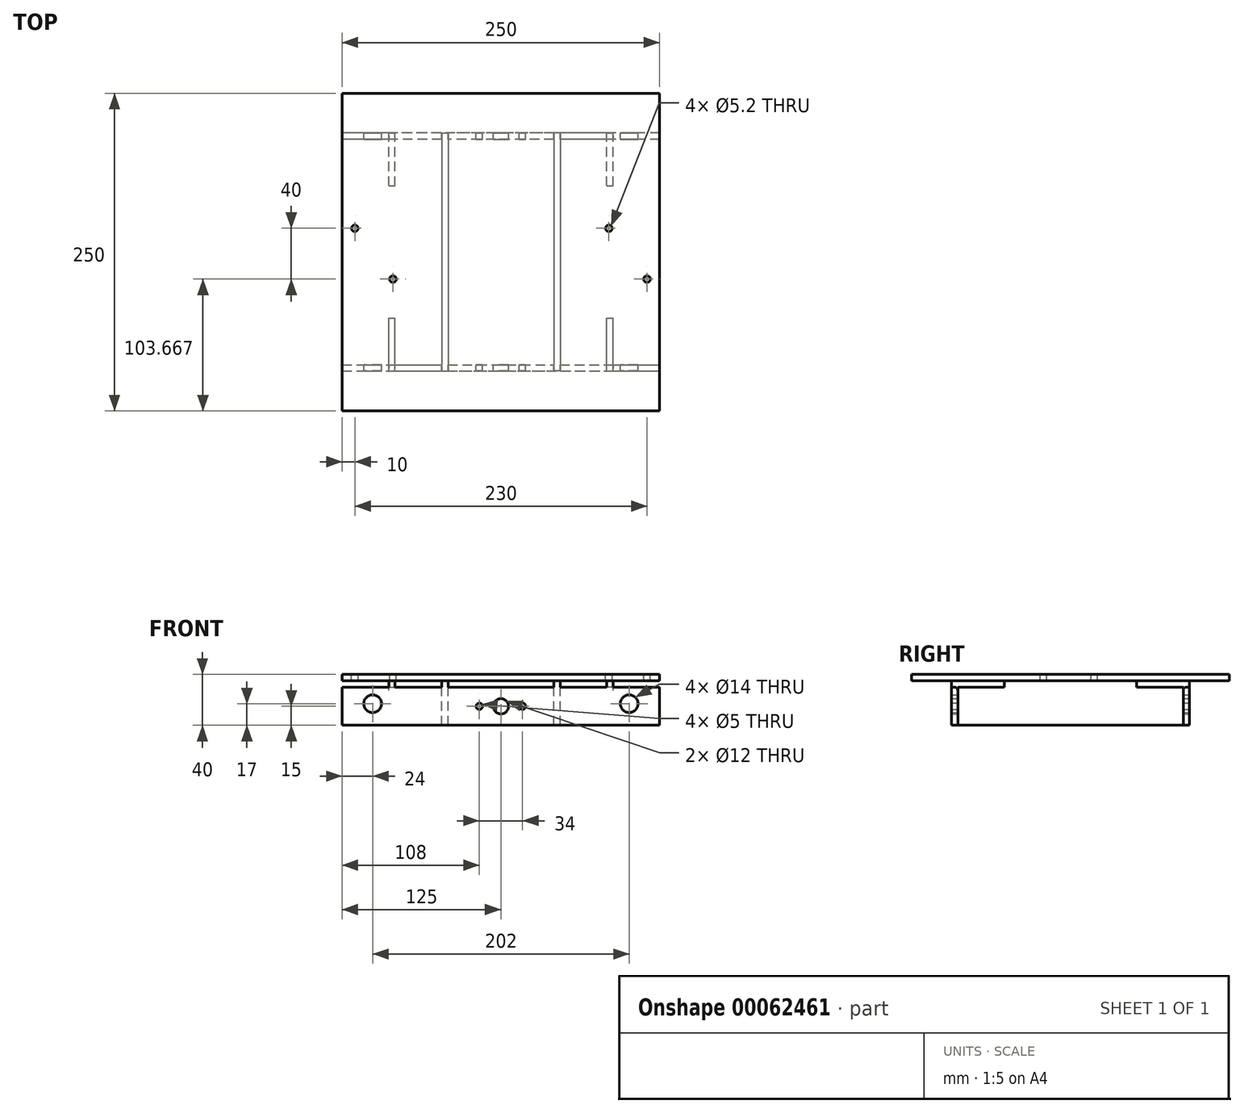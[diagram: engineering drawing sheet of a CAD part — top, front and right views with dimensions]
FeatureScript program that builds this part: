
annotation { "Feature Type Name" : "Feature", "Feature Type Description" : "" }
export const myFeature = defineFeature(function(context is Context, id is Id, definition is map)
    precondition{}
    {
        {
            assignVariable(context, id + "F0", {"name" : "BASE_THICKNESS", "anyValue" : 5});
        }
        {
            assignVariable(context, id + "F1", {"name" : "FLANGE_OFFSET", "anyValue" : 5});
        }
        {
            var Q0;
            Q0=qCreatedBy(makeId("Top.planeOp"),FACE);
            var sketch = newSketch(context, id + "F2", { "sketchPlane" : qUnion([Q0])});
            skLineSegment(sketch, "E0.rect.bottom", {"start": v(125, -125) * mm, "end": v(-125, -125) * mm});
            skLineSegment(sketch, "E0.rect.top", {"start": v(125, 125) * mm, "end": v(-125, 125) * mm});
            skLineSegment(sketch, "E0.rect.left", {"start": v(125, -125) * mm, "end": v(125, 125) * mm});
            skLineSegment(sketch, "E0.rect.right", {"start": v(-125, -125) * mm, "end": v(-125, 125) * mm});
            skPoint(sketch, "E0.rect.middle", {"position": v(0, 0) * mm});
            skSolve(sketch);
        }
        {
            var Q0;
            Q0 = qSketchRegion(id + "F2", true);
            extrude(context, id + "F3", {"entities" : qUnion([Q0]), "depth" : (getVariable(context, 'BASE_THICKNESS')) * mm});
        }
        {
            var Q0;
            Q0=makeQuery(id+"F3.opExtrude","CAP_FACE",FACE,{"disambiguationData":[OSD([sQuery(id+"F2.wireOp",EDGE,"E0.rect.bottom"),sQuery(id+"F2.wireOp",EDGE,"E0.rect.top"),sQuery(id+"F2.wireOp",EDGE,"E0.rect.left"),sQuery(id+"F2.wireOp",EDGE,"E0.rect.right")])],"isStart":true});
            var sketch = newSketch(context, id + "F4", { "sketchPlane" : qUnion([Q0])});
            skLineSegment(sketch, "E1.bottom", {"start": v(-88.33, 93.75) * mm, "end": v(-83.33, 93.75) * mm});
            skLineSegment(sketch, "E1.top", {"start": v(-88.33, 52.08) * mm, "end": v(-83.33, 52.08) * mm});
            skLineSegment(sketch, "E1.left", {"start": v(-88.33, 93.75) * mm, "end": v(-88.33, 52.08) * mm});
            skLineSegment(sketch, "E1.right", {"start": v(-83.33, 93.75) * mm, "end": v(-83.33, 52.08) * mm});
            skLineSegment(sketch, "E2.bottom", {"start": v(83.33, 93.75) * mm, "end": v(88.33, 93.75) * mm});
            skLineSegment(sketch, "E2.top", {"start": v(83.33, 52.08) * mm, "end": v(88.33, 52.08) * mm});
            skLineSegment(sketch, "E2.left", {"start": v(83.33, 93.75) * mm, "end": v(83.33, 52.08) * mm});
            skLineSegment(sketch, "E2.right", {"start": v(88.33, 93.75) * mm, "end": v(88.33, 52.08) * mm});
            skLineSegment(sketch, "E3.bottom", {"start": v(-88.33, -52.08) * mm, "end": v(-83.33, -52.08) * mm});
            skLineSegment(sketch, "E3.top", {"start": v(-88.33, -93.75) * mm, "end": v(-83.33, -93.75) * mm});
            skLineSegment(sketch, "E3.left", {"start": v(-88.33, -52.08) * mm, "end": v(-88.33, -93.75) * mm});
            skLineSegment(sketch, "E3.right", {"start": v(-83.33, -52.08) * mm, "end": v(-83.33, -93.75) * mm});
            skLineSegment(sketch, "E4.bottom", {"start": v(83.33, -52.08) * mm, "end": v(88.33, -52.08) * mm});
            skLineSegment(sketch, "E4.top", {"start": v(83.33, -93.75) * mm, "end": v(88.33, -93.75) * mm});
            skLineSegment(sketch, "E4.left", {"start": v(83.33, -52.08) * mm, "end": v(83.33, -93.75) * mm});
            skLineSegment(sketch, "E4.right", {"start": v(88.33, -52.08) * mm, "end": v(88.33, -93.75) * mm});
            skSolve(sketch);
        }
        {
            var Q0;
            Q0 = qSketchRegion(id + "F4", true);
            extrude(context, id + "F5", {"entities" : qUnion([Q0]), "operationType" : NewBodyOperationType.ADD, "depth" : (getVariable(context, 'FLANGE_OFFSET')) * mm});
        }
        {
            var Q0;
            Q0=makeQuery(id+"F5.opExtrude","SWEPT_FACE",FACE,{"disambiguationData":[OSD([sQuery(id+"F4.wireOp",EDGE,"E4.top")])]});
            var sketch = newSketch(context, id + "F6", { "sketchPlane" : qUnion([Q0])});
            skLineSegment(sketch, "E5.bottom", {"start": v(-125, -5) * mm, "end": v(125, -5) * mm});
            skLineSegment(sketch, "E5.top", {"start": v(-125, -35) * mm, "end": v(125, -35) * mm});
            skLineSegment(sketch, "E5.left", {"start": v(-125, -5) * mm, "end": v(-125, -35) * mm});
            skLineSegment(sketch, "E5.right", {"start": v(125, -5) * mm, "end": v(125, -35) * mm});
            skSolve(sketch);
        }
        {
            var Q0;
            Q0 = qSketchRegion(id + "F6", true);
            extrude(context, id + "F7", {"entities" : qUnion([Q0]), "operationType" : NewBodyOperationType.ADD, "oppositeDirection" : true, "depth" : (getVariable(context, 'BASE_THICKNESS')) * mm});
        }
        {
            var Q0;
            Q0=makeQuery(id+"F5.opExtrude","SWEPT_FACE",FACE,{"disambiguationData":[OSD([sQuery(id+"F4.wireOp",EDGE,"E1.bottom")])]});
            var sketch = newSketch(context, id + "F8", { "sketchPlane" : qUnion([Q0])});
            skPoint(sketch, "E6.firstSnap0", {"position": v(-85.83, -5) * mm});
            skLineSegment(sketch, "E6.bottom", {"start": v(-125, -5) * mm, "end": v(125, -5) * mm});
            skLineSegment(sketch, "E6.top", {"start": v(-125, -35) * mm, "end": v(125, -35) * mm});
            skLineSegment(sketch, "E6.left", {"start": v(-125, -5) * mm, "end": v(-125, -35) * mm});
            skLineSegment(sketch, "E6.right", {"start": v(125, -5) * mm, "end": v(125, -35) * mm});
            skSolve(sketch);
        }
        {
            var Q0;
            Q0 = qSketchRegion(id + "F8", true);
            extrude(context, id + "F9", {"entities" : qUnion([Q0]), "operationType" : NewBodyOperationType.ADD, "oppositeDirection" : true, "depth" : (getVariable(context, 'BASE_THICKNESS')) * mm});
        }
        {
            var Q0;
            Q0=makeQuery(id+"F3.opExtrude","CAP_FACE",FACE,{"disambiguationData":[OSD([sQuery(id+"F2.wireOp",EDGE,"E0.rect.bottom"),sQuery(id+"F2.wireOp",EDGE,"E0.rect.top"),sQuery(id+"F2.wireOp",EDGE,"E0.rect.left"),sQuery(id+"F2.wireOp",EDGE,"E0.rect.right")])],"isStart":true});
            var sketch = newSketch(context, id + "F10", { "sketchPlane" : qUnion([Q0])});
            skLineSegment(sketch, "E7.rect.bottom", {"start": v(46.67, -93.75) * mm, "end": v(41.67, -93.75) * mm});
            skLineSegment(sketch, "E7.rect.top", {"start": v(46.67, 93.75) * mm, "end": v(41.67, 93.75) * mm});
            skLineSegment(sketch, "E7.rect.left", {"start": v(46.67, -93.75) * mm, "end": v(46.67, 93.75) * mm});
            skLineSegment(sketch, "E7.rect.right", {"start": v(41.67, -93.75) * mm, "end": v(41.67, 93.75) * mm});
            skPoint(sketch, "E7.rect.middle", {"position": v(0, 0) * mm});
            skLineSegment(sketch, "E8.MirrorCS", {"start": v(-46.67, -93.75) * mm, "end": v(-46.67, 93.75) * mm});
            skLineSegment(sketch, "E9.MirrorCS", {"start": v(-41.67, -93.75) * mm, "end": v(-41.67, 93.75) * mm});
            skLineSegment(sketch, "E10.MirrorCS", {"start": v(-46.67, -93.75) * mm, "end": v(-41.67, -93.75) * mm});
            skLineSegment(sketch, "E11.MirrorCS", {"start": v(-46.67, 93.75) * mm, "end": v(-41.67, 93.75) * mm});
            skLineSegment(sketch, "E12", {"start": v(46.67, 93.75) * mm, "end": v(41.67, -93.75) * mm, "construction": true});
            skLineSegment(sketch, "E13", {"start": v(41.67, 93.75) * mm, "end": v(46.67, -93.75) * mm, "construction": true});
            skPoint(sketch, "E14", {"position": v(44.17, 0) * mm});
            skSolve(sketch);
        }
        {
            var Q0;
            {var subQ0=sQuery(id+"F8.wireOp",EDGE,"E6.bottom");var subQ1=sQuery(id+"F4.wireOp",EDGE,"E2.right");var subQ2=sQuery(id+"F4.wireOp",EDGE,"E2.left");Q0=makeQuery(id+"F9.boolean.opBoolean","SPLIT",EDGE,{"disambiguationData":[TD([makeQuery(id+"F5.opExtrude","CAP_FACE",FACE,{"disambiguationData":[OSD([sQuery(id+"F4.wireOp",EDGE,"E2.bottom"),sQuery(id+"F4.wireOp",EDGE,"E2.top"),subQ2,subQ1])],"isStart":false}),makeQuery(id+"F5.opExtrude","SWEPT_FACE",FACE,{"disambiguationData":[OSD([subQ2])]}),makeQuery(id+"F5.opExtrude","SWEPT_FACE",FACE,{"disambiguationData":[OSD([subQ1])]}),makeQuery(id+"F9.opExtrude","SWEPT_FACE",FACE,{"disambiguationData":[OSD([subQ0])]}),makeQuery(id+"F9.opExtrude","CAP_FACE",FACE,{"disambiguationData":[OSD([subQ0,sQuery(id+"F8.wireOp",EDGE,"E6.top"),sQuery(id+"F8.wireOp",EDGE,"E6.left"),sQuery(id+"F8.wireOp",EDGE,"E6.right")])],"isStart":false})])],"derivedFrom":makeQuery(id+"F9.opExtrude","CAP_EDGE",EDGE,{"disambiguationData":[OSD([subQ0])],"isStart":false})});}
            var Q1;
            {var subQ0=sQuery(id+"F8.wireOp",EDGE,"E6.bottom");var subQ1=sQuery(id+"F4.wireOp",EDGE,"E1.right");var subQ2=sQuery(id+"F4.wireOp",EDGE,"E1.left");Q1=makeQuery(id+"F9.boolean.opBoolean","SPLIT",EDGE,{"disambiguationData":[TD([makeQuery(id+"F5.opExtrude","CAP_FACE",FACE,{"disambiguationData":[OSD([sQuery(id+"F4.wireOp",EDGE,"E1.bottom"),sQuery(id+"F4.wireOp",EDGE,"E1.top"),subQ2,subQ1])],"isStart":false}),makeQuery(id+"F5.opExtrude","SWEPT_FACE",FACE,{"disambiguationData":[OSD([subQ2])]}),makeQuery(id+"F5.opExtrude","SWEPT_FACE",FACE,{"disambiguationData":[OSD([subQ1])]}),makeQuery(id+"F9.opExtrude","SWEPT_FACE",FACE,{"disambiguationData":[OSD([subQ0])]}),makeQuery(id+"F9.opExtrude","CAP_FACE",FACE,{"disambiguationData":[OSD([subQ0,sQuery(id+"F8.wireOp",EDGE,"E6.top"),sQuery(id+"F8.wireOp",EDGE,"E6.left"),sQuery(id+"F8.wireOp",EDGE,"E6.right")])],"isStart":false})])],"derivedFrom":makeQuery(id+"F9.opExtrude","CAP_EDGE",EDGE,{"disambiguationData":[OSD([subQ0])],"isStart":false})});}
            var Q2;
            {var subQ0=sQuery(id+"F6.wireOp",EDGE,"E5.bottom");var subQ1=sQuery(id+"F4.wireOp",EDGE,"E4.right");var subQ2=sQuery(id+"F4.wireOp",EDGE,"E4.left");Q2=makeQuery(id+"F7.boolean.opBoolean","SPLIT",EDGE,{"disambiguationData":[TD([makeQuery(id+"F5.opExtrude","CAP_FACE",FACE,{"disambiguationData":[OSD([sQuery(id+"F4.wireOp",EDGE,"E4.bottom"),sQuery(id+"F4.wireOp",EDGE,"E4.top"),subQ2,subQ1])],"isStart":false}),makeQuery(id+"F5.opExtrude","SWEPT_FACE",FACE,{"disambiguationData":[OSD([subQ2])]}),makeQuery(id+"F5.opExtrude","SWEPT_FACE",FACE,{"disambiguationData":[OSD([subQ1])]}),makeQuery(id+"F7.opExtrude","SWEPT_FACE",FACE,{"disambiguationData":[OSD([subQ0])]}),makeQuery(id+"F7.opExtrude","CAP_FACE",FACE,{"disambiguationData":[OSD([subQ0,sQuery(id+"F6.wireOp",EDGE,"E5.top"),sQuery(id+"F6.wireOp",EDGE,"E5.left"),sQuery(id+"F6.wireOp",EDGE,"E5.right")])],"isStart":false})])],"derivedFrom":makeQuery(id+"F7.opExtrude","CAP_EDGE",EDGE,{"disambiguationData":[OSD([subQ0])],"isStart":false})});}
            var Q3;
            {var subQ0=sQuery(id+"F6.wireOp",EDGE,"E5.bottom");var subQ1=sQuery(id+"F4.wireOp",EDGE,"E3.right");var subQ2=sQuery(id+"F4.wireOp",EDGE,"E3.left");Q3=makeQuery(id+"F7.boolean.opBoolean","SPLIT",EDGE,{"disambiguationData":[TD([makeQuery(id+"F5.opExtrude","CAP_FACE",FACE,{"disambiguationData":[OSD([sQuery(id+"F4.wireOp",EDGE,"E3.bottom"),sQuery(id+"F4.wireOp",EDGE,"E3.top"),subQ2,subQ1])],"isStart":false}),makeQuery(id+"F5.opExtrude","SWEPT_FACE",FACE,{"disambiguationData":[OSD([subQ2])]}),makeQuery(id+"F5.opExtrude","SWEPT_FACE",FACE,{"disambiguationData":[OSD([subQ1])]}),makeQuery(id+"F7.opExtrude","SWEPT_FACE",FACE,{"disambiguationData":[OSD([subQ0])]}),makeQuery(id+"F7.opExtrude","CAP_FACE",FACE,{"disambiguationData":[OSD([subQ0,sQuery(id+"F6.wireOp",EDGE,"E5.top"),sQuery(id+"F6.wireOp",EDGE,"E5.left"),sQuery(id+"F6.wireOp",EDGE,"E5.right")])],"isStart":false})])],"derivedFrom":makeQuery(id+"F7.opExtrude","CAP_EDGE",EDGE,{"disambiguationData":[OSD([subQ0])],"isStart":false})});}
            fillet(context, id + "F11", {"entities" : qUnion([Q0, Q1, Q2, Q3]), "radius" : (getVariable(context, 'BASE_THICKNESS')) / 2 * mm, "tangentPropagation" : true, "allowEdgeOverflow" : false});
        }
        {
            var Q0;
            Q0 = qSketchRegion(id + "F10", true);
            var Q1;
            Q1=makeQuery(id+"F9.opExtrude","SWEPT_FACE",FACE,{"disambiguationData":[OSD([sQuery(id+"F8.wireOp",EDGE,"E6.top")])]});
            extrude(context, id + "F12", {"entities" : qUnion([Q0]), "operationType" : NewBodyOperationType.ADD, "endBound" : BoundingType.UP_TO_SURFACE, "endBoundEntityFace" : qUnion([Q1]), "depth" : 25 * mm});
        }
        {
            var Q0;
            Q0=makeQuery(id+"F12.boolean.opBoolean","MERGE",FACE,{"derivedFrom":[makeQuery(id+"F7.boolean.opBoolean","MERGE",FACE,{"derivedFrom":[makeQuery(id+"F5.opExtrude","SWEPT_FACE",FACE,{"disambiguationData":[OSD([sQuery(id+"F4.wireOp",EDGE,"E3.top")])]}),makeQuery(id+"F5.opExtrude","SWEPT_FACE",FACE,{"disambiguationData":[OSD([sQuery(id+"F4.wireOp",EDGE,"E4.top")])]}),makeQuery(id+"F7.opExtrude","CAP_FACE",FACE,{"disambiguationData":[OSD([sQuery(id+"F6.wireOp",EDGE,"E5.bottom"),sQuery(id+"F6.wireOp",EDGE,"E5.top"),sQuery(id+"F6.wireOp",EDGE,"E5.left"),sQuery(id+"F6.wireOp",EDGE,"E5.right")])],"isStart":true})]}),makeQuery(id+"F12.opExtrude","SWEPT_FACE",FACE,{"disambiguationData":[OSD([sQuery(id+"F10.wireOp",EDGE,"E7.rect.bottom")])]}),makeQuery(id+"F12.opExtrude","SWEPT_FACE",FACE,{"disambiguationData":[OSD([sQuery(id+"F10.wireOp",EDGE,"E10.MirrorCS")])]})]});
            var sketch = newSketch(context, id + "F13", { "sketchPlane" : qUnion([Q0])});
            skCircle(sketch, "E15", {"center": v(0, -20) * mm, "radius": 6 * mm});
            skPoint(sketch, "E15.centerSnap0", {"position": v(0, -5) * mm});
            skCircle(sketch, "E16", {"center": v(-101, -18) * mm, "radius": 7 * mm});
            skCircle(sketch, "E17", {"center": v(101, -18) * mm, "radius": 7 * mm});
            skCircle(sketch, "E18", {"center": v(17, -20) * mm, "radius": 2.5 * mm});
            skCircle(sketch, "E19", {"center": v(-17, -20) * mm, "radius": 2.5 * mm});
            skSolve(sketch);
        }
        {
            var Q0;
            Q0 = qSketchRegion(id + "F13", true);
            extrude(context, id + "F14", {"entities" : qUnion([Q0]), "operationType" : NewBodyOperationType.REMOVE, "endBound" : BoundingType.THROUGH_ALL, "oppositeDirection" : true, "depth" : 25 * mm});
        }
        {
            var Q0;
            Q0=makeQuery(id+"F3.opExtrude","CAP_FACE",FACE,{"disambiguationData":[OSD([sQuery(id+"F2.wireOp",EDGE,"E0.rect.bottom"),sQuery(id+"F2.wireOp",EDGE,"E0.rect.top"),sQuery(id+"F2.wireOp",EDGE,"E0.rect.left"),sQuery(id+"F2.wireOp",EDGE,"E0.rect.right")])],"isStart":false});
            var sketch = newSketch(context, id + "F15", { "sketchPlane" : qUnion([Q0])});
            skCircle(sketch, "E20", {"center": v(-85, -21.33) * mm, "radius": 2.6 * mm});
            skCircle(sketch, "E21", {"center": v(-115, 18.67) * mm, "radius": 2.6 * mm});
            skCircle(sketch, "E22", {"center": v(115, -21.33) * mm, "radius": 2.6 * mm});
            skCircle(sketch, "E23", {"center": v(85, 18.67) * mm, "radius": 2.6 * mm});
            skSolve(sketch);
        }
        {
            var Q0;
            Q0 = qSketchRegion(id + "F15", true);
            extrude(context, id + "F16", {"entities" : qUnion([Q0]), "operationType" : NewBodyOperationType.REMOVE, "endBound" : BoundingType.THROUGH_ALL, "oppositeDirection" : true, "depth" : 25 * mm});
        }
    });
